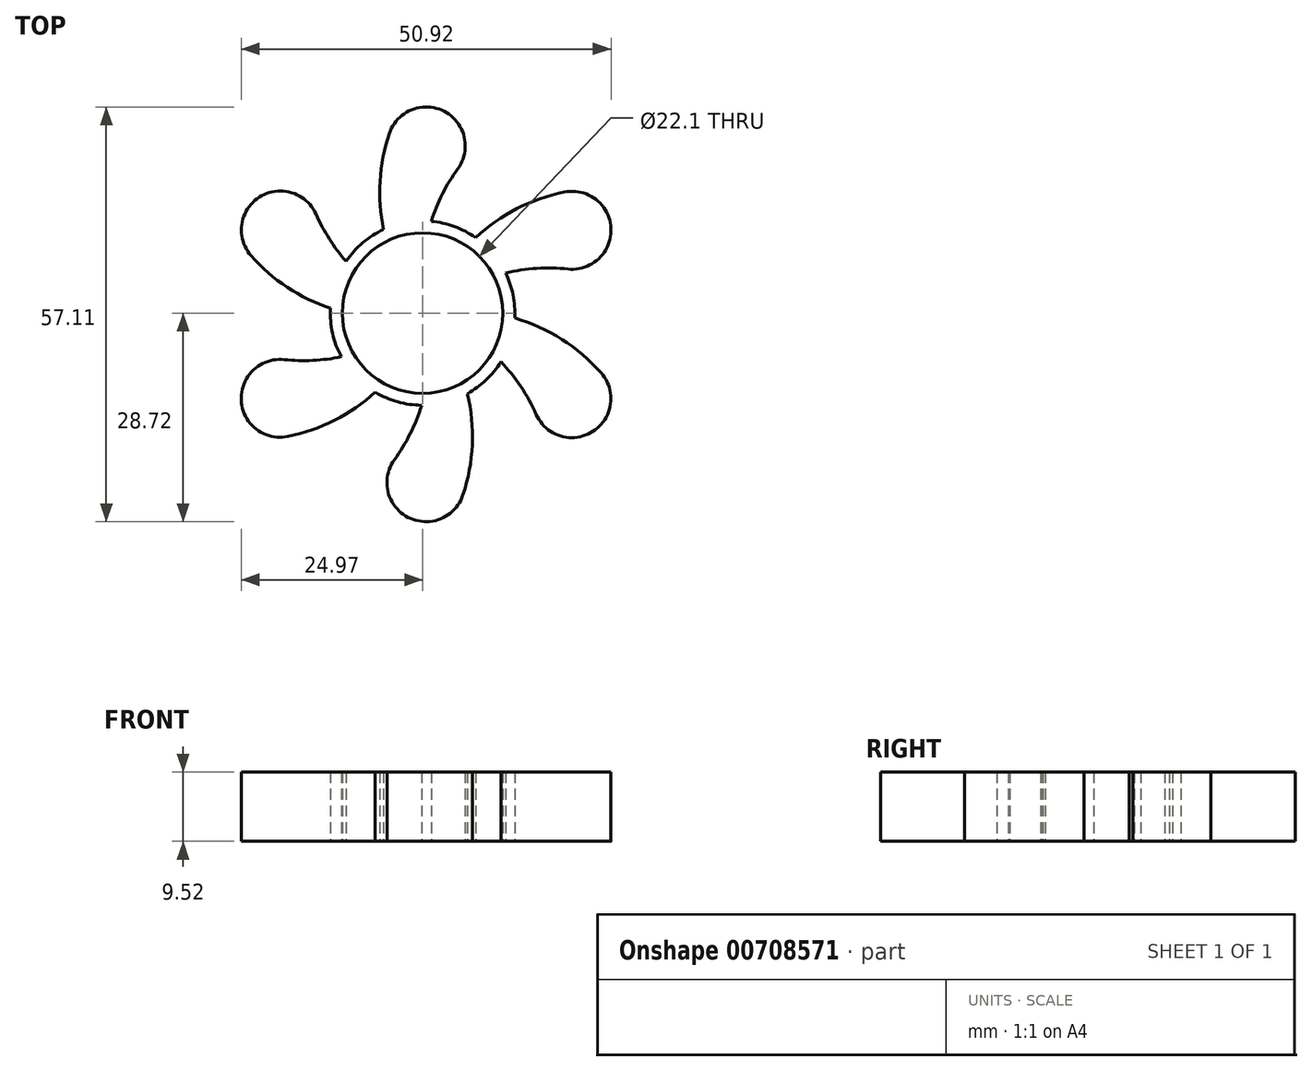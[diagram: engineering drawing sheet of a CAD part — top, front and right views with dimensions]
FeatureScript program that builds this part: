
annotation { "Feature Type Name" : "Feature", "Feature Type Description" : "" }
export const myFeature = defineFeature(function(context is Context, id is Id, definition is map)
    precondition{}
    {
        {
            var Q0;
            Q0=qCreatedBy(makeId("Top.planeOp"),FACE);
            var sketch = newSketch(context, id + "F0", { "sketchPlane" : qUnion([Q0])});
            skArc(sketch, "E0", {"start": v(-12.68, 0.65) * mm, "mid": v(-12.4, -2.79) * mm, "end": v(-11.18, -6.02) * mm});
            skCircle(sketch, "E1", {"center": v(0, 0) * mm, "radius": 11.05 * mm});
            skArc(sketch, "E2.1.0", {"start": v(-23.6, 7.89) * mm, "mid": v(-18.62, 3.55) * mm, "end": v(-12.68, 0.65) * mm});
            skArc(sketch, "E2.3.0", {"start": v(-18.53, -17) * mm, "mid": v(-12.11, -14.76) * mm, "end": v(-6.51, -10.9) * mm});
            skArc(sketch, "E2.5.0", {"start": v(5.55, -25.06) * mm, "mid": v(6.84, -18.12) * mm, "end": v(6.17, -11.1) * mm});
            skArc(sketch, "E2.6.0", {"start": v(15.65, -13.96) * mm, "mid": v(13.53, -10.12) * mm, "end": v(10.79, -6.7) * mm});
            skArc(sketch, "E2.7.0", {"start": v(24.58, -8.23) * mm, "mid": v(19.16, -3.61) * mm, "end": v(12.68, -0.68) * mm});
            skArc(sketch, "E2.9.0", {"start": v(19.5, 16.66) * mm, "mid": v(12.97, 14.37) * mm, "end": v(7.3, 10.4) * mm});
            skPoint(sketch, "E2.center", {"position": v(0.49, -0.17) * mm});
            skArc(sketch, "E3", {"start": v(4.85, 19.86) * mm, "mid": v(2.97, 27.79) * mm, "end": v(-4.58, 24.72) * mm});
            skArc(sketch, "E4.2.11.0", {"start": v(-4.58, 24.72) * mm, "mid": v(-5.85, 18.17) * mm, "end": v(-5.36, 11.51) * mm});
            skArc(sketch, "E5.1.0", {"start": v(-14.67, 13.62) * mm, "mid": v(-22.48, 15.96) * mm, "end": v(-23.6, 7.89) * mm});
            skArc(sketch, "E5.2.0", {"start": v(-19.04, -6.4) * mm, "mid": v(-24.97, -12) * mm, "end": v(-18.53, -17) * mm});
            skArc(sketch, "E5.3.0", {"start": v(-3.87, -20.2) * mm, "mid": v(-2, -28.13) * mm, "end": v(5.55, -25.06) * mm});
            skArc(sketch, "E5.4.0", {"start": v(15.65, -13.96) * mm, "mid": v(23.46, -16.3) * mm, "end": v(24.58, -8.23) * mm});
            skArc(sketch, "E5.5.0", {"start": v(20.01, 6.07) * mm, "mid": v(25.94, 11.66) * mm, "end": v(19.5, 16.66) * mm});
            skPoint(sketch, "E6.orphan", {"position": v(-4.03, 26.22) * mm});
            skArc(sketch, "E7.trimOffspring", {"start": v(4.85, 19.86) * mm, "mid": v(2.73, 16.4) * mm, "end": v(1.19, 12.64) * mm});
            skPoint(sketch, "E8.orphan", {"position": v(21.08, 16.93) * mm});
            skArc(sketch, "E9.trimOffspring", {"start": v(20.01, 6.07) * mm, "mid": v(15.7, 6.16) * mm, "end": v(11.44, 5.52) * mm});
            skPoint(sketch, "E10.orphan", {"position": v(25.6, -9.45) * mm});
            skPoint(sketch, "E11.orphan", {"position": v(17.59, -20.76) * mm});
            skArc(sketch, "E12.trimOffspring", {"start": v(-3.87, -20.2) * mm, "mid": v(-1.69, -16.6) * mm, "end": v(-0.12, -12.7) * mm});
            skArc(sketch, "E13.trimOffspring", {"start": v(-19.04, -6.4) * mm, "mid": v(-15.1, -6.52) * mm, "end": v(-11.18, -6.02) * mm});
            skArc(sketch, "E14.trimOffspring", {"start": v(-14.67, 13.62) * mm, "mid": v(-12.84, 10.21) * mm, "end": v(-10.51, 7.13) * mm});
            skPoint(sketch, "E15.orphan", {"position": v(-24.62, 9.11) * mm});
            skPoint(sketch, "E16.orphan", {"position": v(-20.1, -17.27) * mm});
            skPoint(sketch, "E17.orphan", {"position": v(5, -26.55) * mm});
            skArc(sketch, "E18.trimOffspring", {"start": v(-5.36, 11.51) * mm, "mid": v(-8.23, 9.67) * mm, "end": v(-10.51, 7.13) * mm});
            skArc(sketch, "E19.trimOffspring", {"start": v(7.3, 10.4) * mm, "mid": v(4.39, 11.92) * mm, "end": v(1.19, 12.64) * mm});
            skArc(sketch, "E20.trimOffspring", {"start": v(12.68, -0.68) * mm, "mid": v(12.45, 2.5) * mm, "end": v(11.44, 5.52) * mm});
            skArc(sketch, "E21.trimOffspring", {"start": v(6.17, -11.1) * mm, "mid": v(8.76, -9.2) * mm, "end": v(10.79, -6.7) * mm});
            skArc(sketch, "E22.trimOffspring", {"start": v(-6.51, -10.9) * mm, "mid": v(-3.44, -12.23) * mm, "end": v(-0.12, -12.7) * mm});
            skPoint(sketch, "E23.orphan", {"position": v(0.32, -0.66) * mm});
            skSolve(sketch);
        }
        {
            var Q0;
            Q0 = qSketchRegion(id + "F0", true);
            extrude(context, id + "F1", {"entities" : qUnion([Q0]), "endBound" : BoundingType.SYMMETRIC, "depth" : 9.52 * mm, "offsetDistance" : 25.4 * mm});
        }
    });
